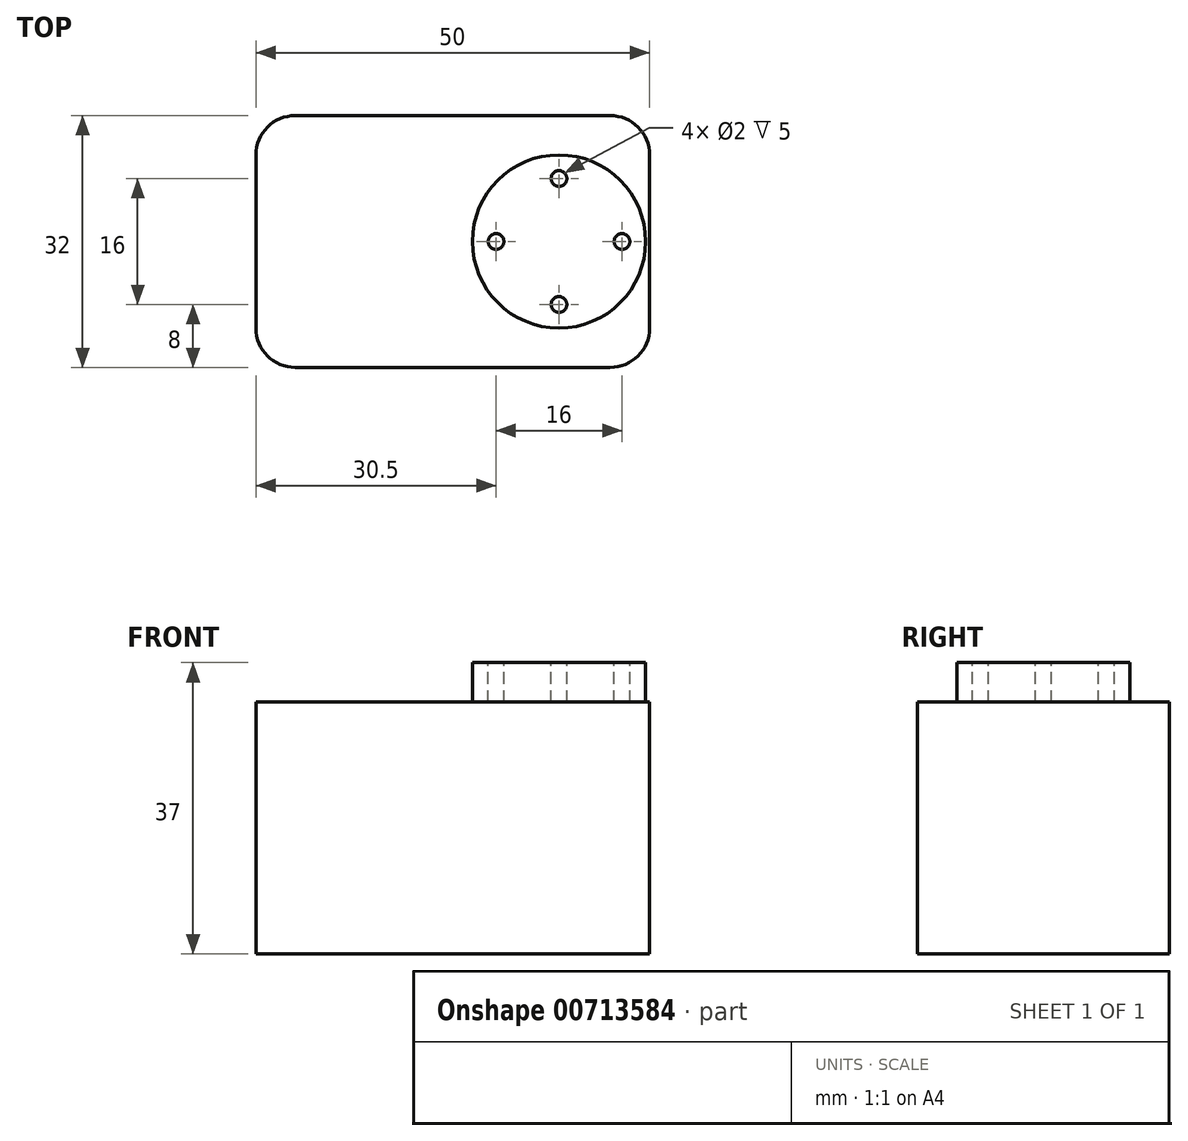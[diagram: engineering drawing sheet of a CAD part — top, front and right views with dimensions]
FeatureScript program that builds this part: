
annotation { "Feature Type Name" : "Feature", "Feature Type Description" : "" }
export const myFeature = defineFeature(function(context is Context, id is Id, definition is map)
    precondition{}
    {
        {
            var Q0;
            Q0=qCreatedBy(makeId("Top.planeOp"),FACE);
            var sketch = newSketch(context, id + "F0", { "sketchPlane" : qUnion([Q0])});
            skLineSegment(sketch, "E0.bottom", {"start": v(25, -16) * mm, "end": v(-25, -16) * mm});
            skLineSegment(sketch, "E0.top", {"start": v(25, 16) * mm, "end": v(-25, 16) * mm});
            skLineSegment(sketch, "E0.left", {"start": v(25, -16) * mm, "end": v(25, 16) * mm});
            skLineSegment(sketch, "E0.right", {"start": v(-25, -16) * mm, "end": v(-25, 16) * mm});
            skPoint(sketch, "E0.middle", {"position": v(0, 0) * mm});
            skSolve(sketch);
        }
        {
            var Q0;
            Q0=makeQuery(id+"F0.imprint","IMPRINT",FACE,{"disambiguationData":[TD([[makeQuery(id+"F0.imprint","IMPRINT",EDGE,{"derivedFrom":sQuery(id+"F0.wireOp",EDGE,"E0.bottom")}),-1.0]])]});
            extrude(context, id + "F1", {"entities" : qUnion([Q0]), "depth" : 32 * mm});
        }
        {
            var Q0;
            Q0=makeQuery(id+"F1.opExtrude","SWEPT_EDGE",EDGE,{"disambiguationData":[OSD([sQuery(id+"F0.wireOp",EDGE,"E0.bottom"),sQuery(id+"F0.wireOp",EDGE,"E0.right")])]});
            var Q1;
            Q1=makeQuery(id+"F1.opExtrude","SWEPT_EDGE",EDGE,{"disambiguationData":[OSD([sQuery(id+"F0.wireOp",EDGE,"E0.top"),sQuery(id+"F0.wireOp",EDGE,"E0.right")])]});
            var Q2;
            Q2=makeQuery(id+"F1.opExtrude","SWEPT_EDGE",EDGE,{"disambiguationData":[OSD([sQuery(id+"F0.wireOp",EDGE,"E0.bottom"),sQuery(id+"F0.wireOp",EDGE,"E0.left")])]});
            var Q3;
            Q3=makeQuery(id+"F1.opExtrude","SWEPT_EDGE",EDGE,{"disambiguationData":[OSD([sQuery(id+"F0.wireOp",EDGE,"E0.top"),sQuery(id+"F0.wireOp",EDGE,"E0.left")])]});
            fillet(context, id + "F2", {"entities" : qUnion([Q0, Q1, Q2, Q3]), "radius" : 5 * mm, "tangentPropagation" : true, "allowEdgeOverflow" : false});
        }
        {
            var Q0;
            Q0=makeQuery(id+"F1.opExtrude","CAP_FACE",FACE,{"disambiguationData":[OSD([sQuery(id+"F0.wireOp",EDGE,"E0.bottom"),sQuery(id+"F0.wireOp",EDGE,"E0.top"),sQuery(id+"F0.wireOp",EDGE,"E0.left"),sQuery(id+"F0.wireOp",EDGE,"E0.right")])],"isStart":false});
            var sketch = newSketch(context, id + "F3", { "sketchPlane" : qUnion([Q0])});
            skLineSegment(sketch, "E1", {"start": v(25, 0) * mm, "end": v(13.5, 0) * mm, "construction": true});
            skPoint(sketch, "E1.endSnap0", {"position": v(25, 0) * mm});
            skCircle(sketch, "E2", {"center": v(13.5, 0) * mm, "radius": 11 * mm});
            skSolve(sketch);
        }
        {
            var Q0;
            Q0=makeQuery(id+"F3.imprint","IMPRINT",FACE,{"disambiguationData":[TD([[makeQuery(id+"F3.imprint","IMPRINT",EDGE,{"derivedFrom":sQuery(id+"F3.wireOp",EDGE,"E2")}),1.0]])]});
            extrude(context, id + "F4", {"entities" : qUnion([Q0]), "operationType" : NewBodyOperationType.ADD, "depth" : 5 * mm});
        }
        {
            var Q0;
            Q0=makeQuery(id+"F4.opExtrude","CAP_FACE",FACE,{"disambiguationData":[OSD([sQuery(id+"F3.wireOp",EDGE,"E2")])],"isStart":false});
            var sketch = newSketch(context, id + "F5", { "sketchPlane" : qUnion([Q0])});
            skCircle(sketch, "E3", {"center": v(13.5, 0) * mm, "radius": 8 * mm, "construction": true});
            skCircle(sketch, "E4", {"center": v(21.5, 0) * mm, "radius": 1 * mm});
            skCircle(sketch, "E5", {"center": v(13.5, 8) * mm, "radius": 1 * mm});
            skCircle(sketch, "E6", {"center": v(5.5, 0) * mm, "radius": 1 * mm});
            skCircle(sketch, "E7", {"center": v(13.5, -8) * mm, "radius": 1 * mm});
            skSolve(sketch);
        }
        {
            var Q0;
            Q0=qSketchRegion(id+"F5",true);
            extrude(context, id + "F6", {"entities" : qUnion([Q0]), "operationType" : NewBodyOperationType.REMOVE, "oppositeDirection" : true, "depth" : 5 * mm});
        }
    });
